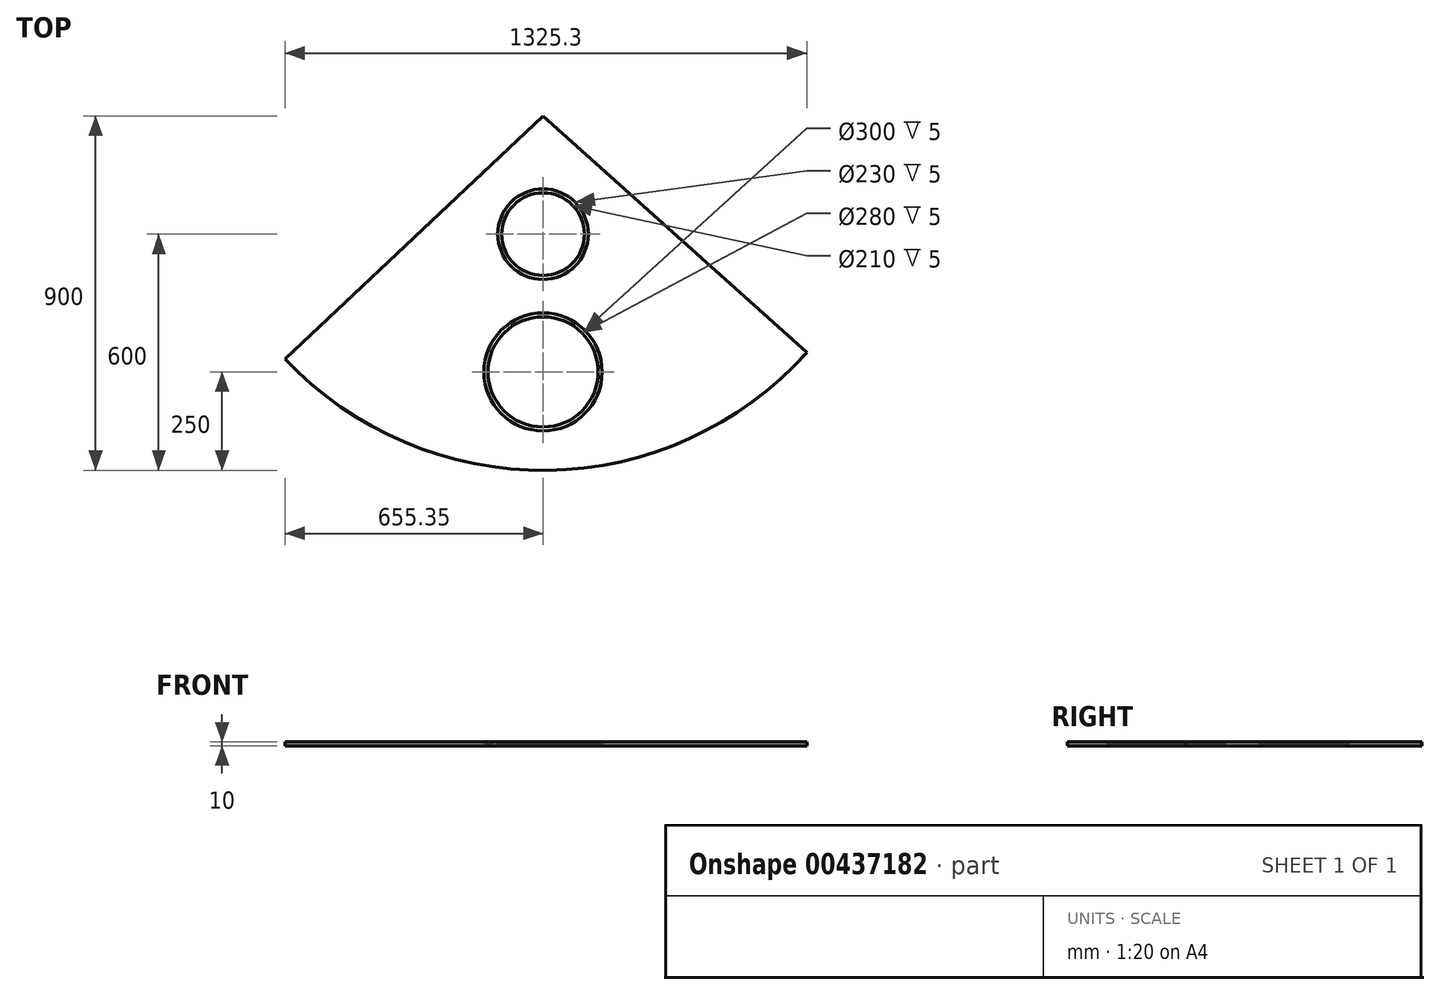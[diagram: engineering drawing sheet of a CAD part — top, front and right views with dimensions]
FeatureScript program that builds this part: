
annotation { "Feature Type Name" : "Feature", "Feature Type Description" : "" }
export const myFeature = defineFeature(function(context is Context, id is Id, definition is map)
    precondition{}
    {
        {
            var Q0;
            Q0=qCreatedBy(makeId("Top.planeOp"),FACE);
            var sketch = newSketch(context, id + "F0", { "sketchPlane" : qUnion([Q0])});
            skPoint(sketch, "E0.middle", {"position": v(0, 0) * mm});
            skCircle(sketch, "E1", {"center": v(0, 0) * mm, "radius": 150 * mm});
            skCircle(sketch, "E2", {"center": v(0, 0) * mm, "radius": 140 * mm});
            skLineSegment(sketch, "E3", {"start": v(669.95, 49.02) * mm, "end": v(0, 650) * mm});
            skLineSegment(sketch, "E4", {"start": v(0, 650) * mm, "end": v(-655.35, 33.14) * mm});
            skArc(sketch, "E5", {"start": v(-655.35, 33.14) * mm, "mid": v(10.79, -249.94) * mm, "end": v(669.95, 49.02) * mm});
            skCircle(sketch, "E6", {"center": v(0, 350) * mm, "radius": 115 * mm});
            skCircle(sketch, "E7", {"center": v(0, 350) * mm, "radius": 105 * mm});
            skLineSegment(sketch, "E8", {"start": v(0, 650) * mm, "end": v(0, 0) * mm, "construction": true});
            skSolve(sketch);
        }
        {
            var Q0;
            Q0=makeQuery(id+"F0.imprint","IMPRINT",FACE,{"disambiguationData":[TD([[makeQuery(id+"F0.imprint","IMPRINT",EDGE,{"derivedFrom":sQuery(id+"F0.wireOp",EDGE,"E1")}),-1.0]])]});
            extrude(context, id + "F1", {"entities" : qUnion([Q0]), "depth" : 10 * mm});
        }
        {
            var Q0;
            Q0=makeQuery(id+"F0.imprint","IMPRINT",FACE,{"disambiguationData":[TD([[makeQuery(id+"F0.imprint","IMPRINT",EDGE,{"derivedFrom":sQuery(id+"F0.wireOp",EDGE,"E1")}),1.0]])]});
            var Q1;
            Q1=makeQuery(id+"F0.imprint","IMPRINT",FACE,{"disambiguationData":[TD([[makeQuery(id+"F0.imprint","IMPRINT",EDGE,{"derivedFrom":sQuery(id+"F0.wireOp",EDGE,"E6")}),1.0]])]});
            extrude(context, id + "F2", {"entities" : qUnion([Q0, Q1]), "operationType" : NewBodyOperationType.ADD, "depth" : 5 * mm});
        }
    });
